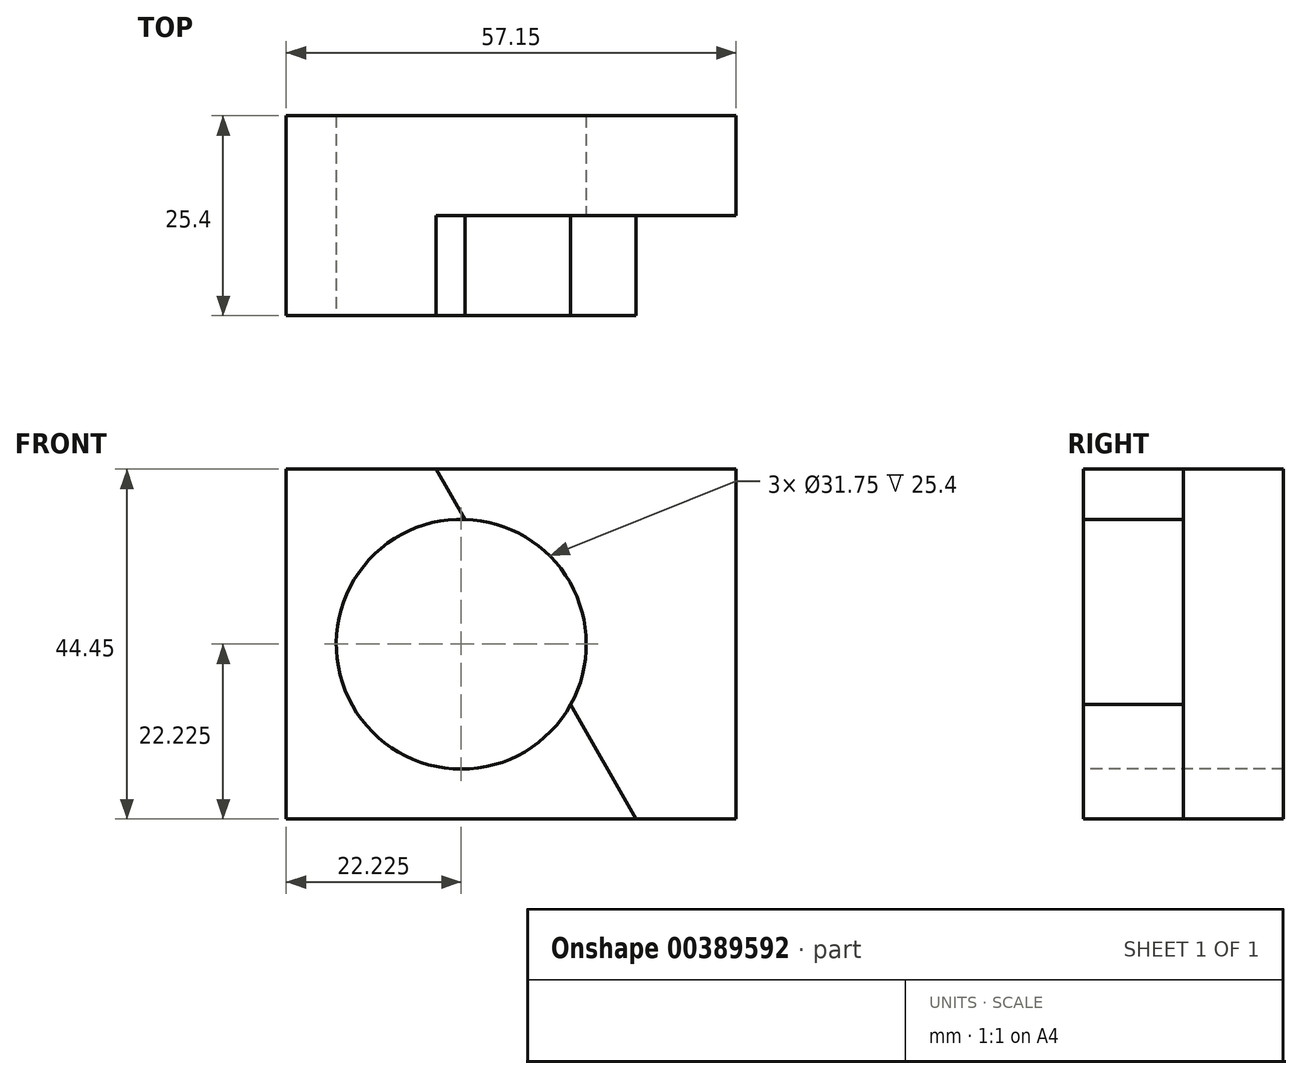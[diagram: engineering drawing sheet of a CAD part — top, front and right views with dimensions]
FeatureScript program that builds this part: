
annotation { "Feature Type Name" : "Feature", "Feature Type Description" : "" }
export const myFeature = defineFeature(function(context is Context, id is Id, definition is map)
    precondition{}
    {
        {
            var Q0;
            Q0=qCreatedBy(makeId("Front.planeOp"),FACE);
            var sketch = newSketch(context, id + "F0", { "sketchPlane" : qUnion([Q0])});
            skLineSegment(sketch, "E0.bottom", {"start": v(0, 44.45) * mm, "end": v(57.15, 44.45) * mm});
            skLineSegment(sketch, "E0.top", {"start": v(0, 0) * mm, "end": v(57.15, 0) * mm});
            skLineSegment(sketch, "E0.left", {"start": v(0, 44.45) * mm, "end": v(0, 0) * mm});
            skLineSegment(sketch, "E0.right", {"start": v(57.15, 44.45) * mm, "end": v(57.15, 0) * mm});
            skSolve(sketch);
        }
        {
            var Q0;
            Q0=makeQuery(id+"F0.imprint","IMPRINT",FACE,{"disambiguationData":[TD([[makeQuery(id+"F0.imprint","IMPRINT",EDGE,{"derivedFrom":sQuery(id+"F0.wireOp",EDGE,"E0.bottom")}),-1.0]])]});
            var sketch = newSketch(context, id + "F1", { "sketchPlane" : qUnion([Q0])});
            skSolve(sketch);
        }
        {
            var Q0;
            Q0 = qSketchRegion(id + "F1", true);
            var Q1;
            Q1=makeQuery(id+"F0.imprint","IMPRINT",FACE,{"disambiguationData":[TD([[makeQuery(id+"F0.imprint","IMPRINT",EDGE,{"derivedFrom":sQuery(id+"F0.wireOp",EDGE,"E0.bottom")}),-1.0]])]});
            extrude(context, id + "F2", {"entities" : qUnion([Q0, Q1]), "depth" : 25.4 * mm});
        }
        {
            var Q0;
            Q0=makeQuery(id+"F2.opExtrude","CAP_FACE",FACE,{"disambiguationData":[OSD([sQuery(id+"F0.wireOp",EDGE,"E0.bottom"),sQuery(id+"F0.wireOp",EDGE,"E0.top"),sQuery(id+"F0.wireOp",EDGE,"E0.left"),sQuery(id+"F0.wireOp",EDGE,"E0.right")])],"isStart":false});
            var sketch = newSketch(context, id + "F3", { "sketchPlane" : qUnion([Q0])});
            skLineSegment(sketch, "E1", {"start": v(44.45, 0) * mm, "end": v(19.05, 44.45) * mm});
            skSolve(sketch);
        }
        {
            var Q0;
            {var subQ0=sQuery(id+"F3.wireOp",EDGE,"E1");Q0=makeQuery(id+"F3.imprint","IMPRINT",FACE,{"disambiguationData":[TD([[makeQuery(id+"F3.imprint","IMPRINT",EDGE,{"derivedFrom":subQ0}),-1.0]])]});}
            extrude(context, id + "F4", {"entities" : qUnion([Q0]), "operationType" : NewBodyOperationType.REMOVE, "oppositeDirection" : true, "depth" : 12.7 * mm});
        }
        {
            var Q0;
            Q0=makeQuery(id+"F2.opExtrude","CAP_FACE",FACE,{"disambiguationData":[OSD([sQuery(id+"F0.wireOp",EDGE,"E0.bottom"),sQuery(id+"F0.wireOp",EDGE,"E0.top"),sQuery(id+"F0.wireOp",EDGE,"E0.left"),sQuery(id+"F0.wireOp",EDGE,"E0.right")])],"isStart":false});
            var sketch = newSketch(context, id + "F5", { "sketchPlane" : qUnion([Q0])});
            skCircle(sketch, "E2", {"center": v(22.23, 22.23) * mm, "radius": 15.87 * mm});
            skPoint(sketch, "E2.centerSnap0", {"position": v(31.75, 22.23) * mm});
            skSolve(sketch);
        }
        {
            var Q0;
            {var subQ0=sQuery(id+"F5.wireOp",EDGE,"E2");var subQ1=makeQuery(id+"F4.boolean.opBoolean","COPY",EDGE,{"derivedFrom":makeQuery(id+"F4.opExtrude","CAP_EDGE",EDGE,{"disambiguationData":[OSD([sQuery(id+"F3.wireOp",EDGE,"E1")])],"isStart":true})});var subQ2=makeQuery(id+"F5.imprint","INTERSECT",VERTEX,{"disambiguationData":[OD(0.0)],"derivedFrom":[subQ1,subQ0]});Q0=makeQuery(id+"F5.imprint","IMPRINT",FACE,{"disambiguationData":[TD([[makeQuery(id+"F5.imprint","IMPRINT",EDGE,{"disambiguationData":[TD([[subQ2,1.0]])],"derivedFrom":subQ0}),1.0]])]});}
            var Q1;
            {var subQ0=sQuery(id+"F5.wireOp",EDGE,"E2");var subQ1=makeQuery(id+"F4.boolean.opBoolean","COPY",EDGE,{"derivedFrom":makeQuery(id+"F4.opExtrude","CAP_EDGE",EDGE,{"disambiguationData":[OSD([sQuery(id+"F3.wireOp",EDGE,"E1")])],"isStart":true})});var subQ2=makeQuery(id+"F5.imprint","INTERSECT",VERTEX,{"disambiguationData":[OD(0.0)],"derivedFrom":[subQ1,subQ0]});Q1=makeQuery(id+"F5.imprint","IMPRINT",FACE,{"disambiguationData":[TD([[makeQuery(id+"F5.imprint","IMPRINT",EDGE,{"disambiguationData":[TD([[subQ2,-1.0]])],"derivedFrom":subQ0}),1.0]])]});}
            extrude(context, id + "F6", {"entities" : qUnion([Q0, Q1]), "operationType" : NewBodyOperationType.REMOVE, "oppositeDirection" : true, "depth" : 25.4 * mm});
        }
    });
